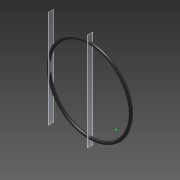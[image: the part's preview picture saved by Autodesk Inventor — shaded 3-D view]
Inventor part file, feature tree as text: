
AUTODESK INVENTOR PART (.ipt)
format: ipt  version: 2015 (Build 190159000, 159)  size: 150,016 bytes
history: native  units: mm
features: other x3, sketch x2, revolve x1, hole x1
ambient origin geometry x8: Origin, YZ Plane, XZ Plane, XY Plane, X Axis, Y Axis, Z Axis, Center Point
bodies: Body1 (feature_tree)
feature tree (7):
  other  "Bryła1"
  revolve  "Obrót1"
  other  "Płaszczyzna do otworu na wentyl 1"
  other  "Płaszczyzna do otworu na wentyl 1.1"
  hole  "Otwór na wentyl"  [1 undecoded]
  sketch  "Szkic1"
  sketch  "Szkic4"
note: 1 required parameter value undecoded (feature->parameter linkage not recoverable at this tier; creation-order binding heuristic only, values carry confidence <= 0.55)
